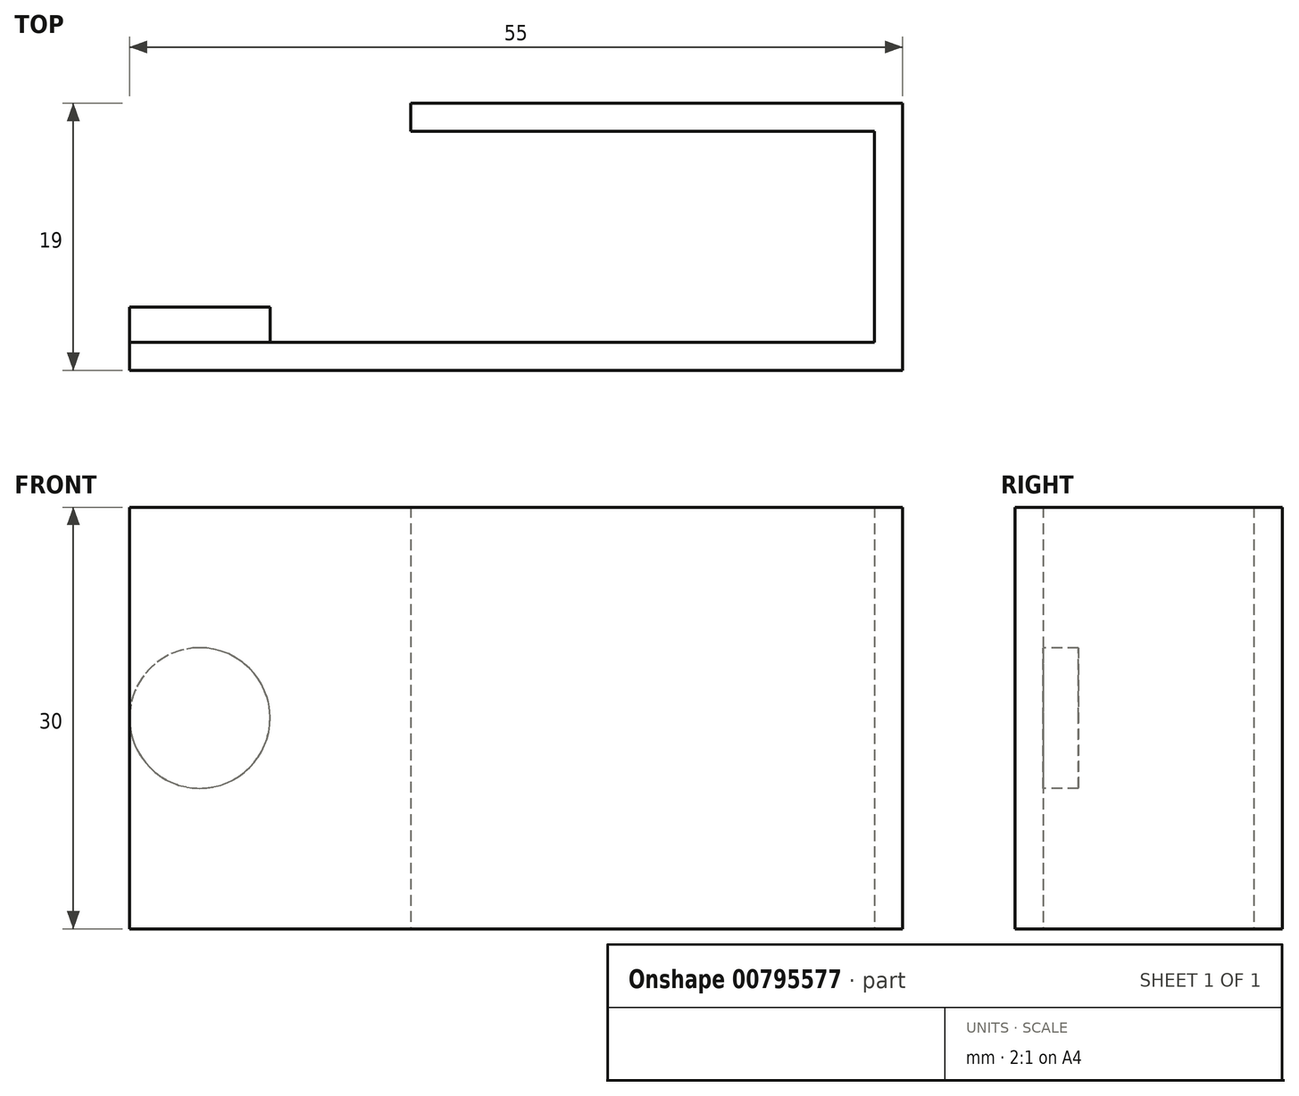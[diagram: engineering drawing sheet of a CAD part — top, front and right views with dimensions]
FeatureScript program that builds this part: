
annotation { "Feature Type Name" : "Feature", "Feature Type Description" : "" }
export const myFeature = defineFeature(function(context is Context, id is Id, definition is map)
    precondition{}
    {
        {
            var Q0;
            Q0=qCreatedBy(makeId("Top.planeOp"),FACE);
            var sketch = newSketch(context, id + "F0", { "sketchPlane" : qUnion([Q0])});
            skLineSegment(sketch, "E0", {"start": v(0, 0) * mm, "end": v(55, 0) * mm});
            skLineSegment(sketch, "E1", {"start": v(55, 0) * mm, "end": v(55, 19) * mm});
            skLineSegment(sketch, "E2", {"start": v(55, 19) * mm, "end": v(20, 19) * mm});
            skLineSegment(sketch, "E3.0", {"start": v(53, 17) * mm, "end": v(20, 17) * mm});
            skLineSegment(sketch, "E3.1", {"start": v(53, 2) * mm, "end": v(53, 17) * mm});
            skLineSegment(sketch, "E3.2", {"start": v(0, 2) * mm, "end": v(53, 2) * mm});
            skLineSegment(sketch, "E4", {"start": v(20, 19) * mm, "end": v(20, 17) * mm});
            skLineSegment(sketch, "E5", {"start": v(0, 2) * mm, "end": v(0, 0) * mm});
            skSolve(sketch);
        }
        {
            var Q0;
            Q0 = qSketchRegion(id + "F0", true);
            extrude(context, id + "F1", {"entities" : qUnion([Q0]), "depth" : 30 * mm, "offsetDistance" : 25.4 * mm});
        }
        {
            var Q0;
            Q0=makeQuery(id+"F1.opExtrude","SWEPT_FACE",FACE,{"disambiguationData":[OSD([sQuery(id+"F0.wireOp",EDGE,"E3.2")])]});
            var sketch = newSketch(context, id + "F2", { "sketchPlane" : qUnion([Q0])});
            skCircle(sketch, "E6", {"center": v(-5, 15) * mm, "radius": 5 * mm});
            skLineSegment(sketch, "E7", {"start": v(-5, 15) * mm, "end": v(0, 15) * mm, "construction": true});
            skSolve(sketch);
        }
        {
            var Q0;
            Q0 = qSketchRegion(id + "F2", true);
            extrude(context, id + "F3", {"entities" : qUnion([Q0]), "operationType" : NewBodyOperationType.ADD, "depth" : 2.5 * mm, "offsetDistance" : 25.4 * mm});
        }
    });
